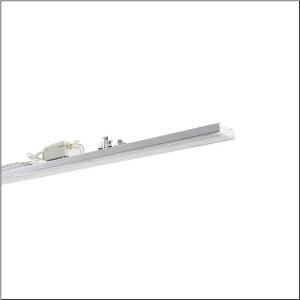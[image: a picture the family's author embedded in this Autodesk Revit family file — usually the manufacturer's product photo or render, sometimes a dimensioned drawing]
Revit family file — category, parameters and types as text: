
# Revit family: licross_r__21_recessed_mo_52tl10cn49xg_3ade
name_source: partatom
category: Lighting Fixtures
units: mm (PartAtom-declared; Revit-internal decimal feet)

## family parameters
Cut with Voids When Loaded = No
Host = Face
Light Source = No
Part Type = Normal
Room Calculation Point = No
Round Connector Dimension = Use Diameter
Shared = No

## types (1)
- --- (1 x LED, 9010 lm, 49.9 W, 4000K)
    Apparent Load = 50 VA
    CIE Flux Codes = 50 81 96 100 100
    Color Rendering = 80
    Color Temperature = 4000K
    Default Elevation = 1800 mm
    Description = Licross® 21 Recessed MO, luminaire insert, of sheet steel, galvanised, coil coated, white, length: 1.500mm, width: 66mm, height: 67mm, LED rated luminous flux: 9.010lm, light colour: 840, control gear: ON/OFF Multilumen, CLOi, control gear: ECG Multilumen, with plug, 3-pole, with phase selection, mains connection: 220..240V, AC, 50/60Hz, start of lifetime: 49W, end of service life: 61W, halogen-free wiring, primary optical cover: cover, of PMMA, light emission: direct distribution, primary light characteristic: symmetric, protection rating (complete): IP40, insulation class (complete): insulation class I (protective earthing), certification: CE, ENEC, VDE, UKCA, protection symbol: D if used in an environment without relevant dust loads with corresponding accessories, impact resistance: IK06, permissible ambient temperature for indoor applications: -35..+40°C, corresponds to IFS (International Featured Standards) requirements for safety and quality in the food industry, reducing of maximum allowable ambient temperature of 5°C with ceiling mounting, LABS conformity tested according to VDMA 24364:2018-05, packaging unit: 1 piece
    Height = 58 mm
    Lamp = 1 x LED
    Lamp Light Flux = 9010 lm
    Lamp Power = 49.9 W
    Lamp count = 1
    Length = 1500 mm
    Luminous efficacy = 181 lm/W
    Manufacturer = Siteco
    ModVariant = No
    Model = 52TL10CN49XG
    Mounting Place = Ceiling
    Mounting Type = Pendant
    Number of Poles = 1
    OnlyDefault = Yes
    Power Factor = 1
    Product Name = Licross® 21 Recessed MO
    Product group = luminaire insert
    ProductGroupID = 901
    Protection Class = Protection class I
    Protection Degree = IP 40
    RLX_Detail_Level = 1
    RLX_Emergency_Light_Flux = 0 lm
    RLX_Emergency_Type = 0
    RLX_Emergency_Type_DB = No
    RlxData = <blob elided: 22153 chars, md5=27ed507e>
    Socket = socket
    Standby Power = 0 W
    System Light Flux = 9010 lm
    System Power = 50 W
    Type Comments = factory setting: luminous flux: 100 % | (A | C | E) | 116 mA
    Type Image = l_1296930.jpg
    URL = http://relux.com
    VarID = @adj_040833
    Voltage = 0 V
    Weight = 0.00 kg
    Width = 66 mm

## geometry (parser evidence)
native form markers: Blend x4, Sweep x10
no freeform markers — native parametric forms only
